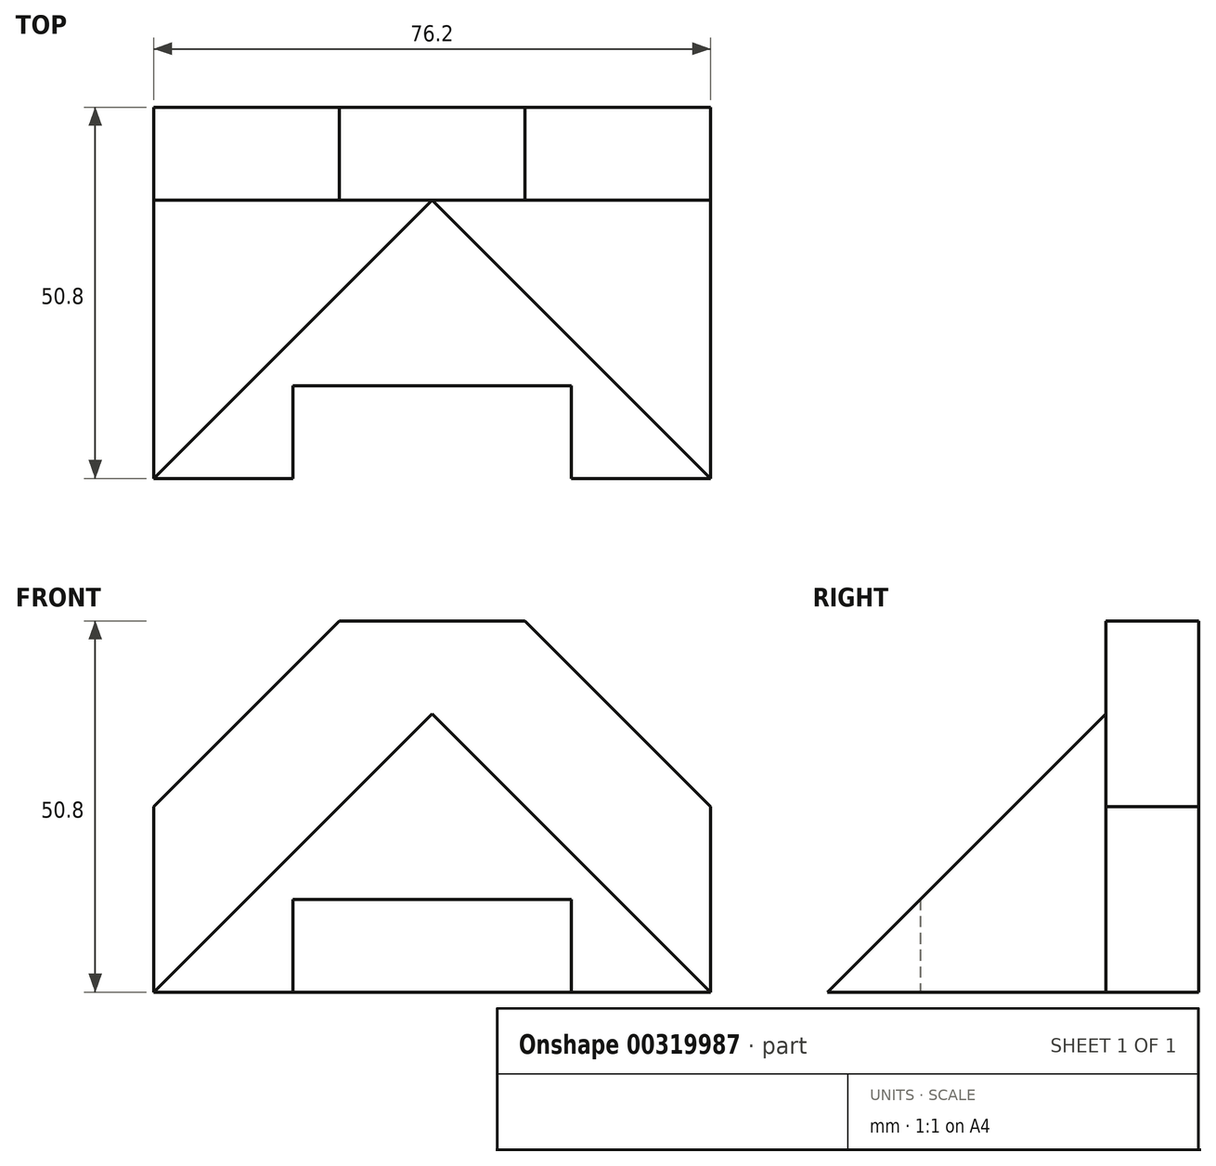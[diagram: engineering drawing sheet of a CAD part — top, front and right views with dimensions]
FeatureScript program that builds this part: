
annotation { "Feature Type Name" : "Feature", "Feature Type Description" : "" }
export const myFeature = defineFeature(function(context is Context, id is Id, definition is map)
    precondition{}
    {
        {
            var Q0;
            Q0=qCreatedBy(makeId("Front.planeOp"),FACE);
            var sketch = newSketch(context, id + "F0", { "sketchPlane" : qUnion([Q0])});
            skLineSegment(sketch, "E0", {"start": v(0, 0) * mm, "end": v(0, 25.4) * mm});
            skLineSegment(sketch, "E1", {"start": v(0, 25.4) * mm, "end": v(25.4, 50.8) * mm});
            skLineSegment(sketch, "E2", {"start": v(25.4, 50.8) * mm, "end": v(50.8, 50.8) * mm});
            skLineSegment(sketch, "E3", {"start": v(50.8, 50.8) * mm, "end": v(76.2, 25.4) * mm});
            skLineSegment(sketch, "E4", {"start": v(76.2, 25.4) * mm, "end": v(76.2, 0) * mm});
            skLineSegment(sketch, "E5", {"start": v(76.2, 0) * mm, "end": v(0, 0) * mm});
            skLineSegment(sketch, "E6", {"start": v(0, 0) * mm, "end": v(38.1, 38.1) * mm});
            skLineSegment(sketch, "E7", {"start": v(38.1, 38.1) * mm, "end": v(76.2, 0) * mm});
            skLineSegment(sketch, "E8", {"start": v(38.1, 50.8) * mm, "end": v(38.1, 0) * mm, "construction": true});
            skSolve(sketch);
        }
        {
            var Q0;
            Q0=makeQuery(id+"F0.imprint","IMPRINT",FACE,{"disambiguationData":[TD([[makeQuery(id+"F0.imprint","IMPRINT",EDGE,{"derivedFrom":sQuery(id+"F0.wireOp",EDGE,"E0")}),-1.0]])]});
            extrude(context, id + "F1", {"entities" : qUnion([Q0]), "depth" : 12.7 * mm});
        }
        {
            var Q0;
            Q0=makeQuery(id+"F0.imprint","IMPRINT",FACE,{"disambiguationData":[TD([[makeQuery(id+"F0.imprint","IMPRINT",EDGE,{"derivedFrom":sQuery(id+"F0.wireOp",EDGE,"E5")}),-1.0]])]});
            extrude(context, id + "F2", {"entities" : qUnion([Q0]), "operationType" : NewBodyOperationType.ADD, "depth" : 50.8 * mm});
        }
        {
            var Q0;
            Q0=qCreatedBy(makeId("Top.planeOp"),FACE);
            var sketch = newSketch(context, id + "F3", { "sketchPlane" : qUnion([Q0])});
            skLineSegment(sketch, "E9.bottom", {"start": v(19.05, -50.8) * mm, "end": v(57.15, -50.8) * mm});
            skLineSegment(sketch, "E9.top", {"start": v(19.05, -38.1) * mm, "end": v(57.15, -38.1) * mm});
            skLineSegment(sketch, "E9.left", {"start": v(19.05, -50.8) * mm, "end": v(19.05, -38.1) * mm});
            skLineSegment(sketch, "E9.right", {"start": v(57.15, -50.8) * mm, "end": v(57.15, -38.1) * mm});
            skSolve(sketch);
        }
        {
            var Q0;
            Q0=makeQuery(id+"F3.imprint","IMPRINT",FACE,{"disambiguationData":[TD([[makeQuery(id+"F3.imprint","IMPRINT",EDGE,{"derivedFrom":sQuery(id+"F3.wireOp",EDGE,"E9.bottom")}),1.0]])]});
            extrude(context, id + "F4", {"entities" : qUnion([Q0]), "operationType" : NewBodyOperationType.REMOVE, "depth" : 12.7 * mm});
        }
        {
            var Q0;
            {var subQ0=sQuery(id+"F0.wireOp",EDGE,"E5");var subQ1=sQuery(id+"F0.wireOp",EDGE,"E7");Q0=makeQuery(id+"F4.boolean.opBoolean","SPLIT",EDGE,{"disambiguationData":[TD([makeQuery(id+"F2.opExtrude","SWEPT_FACE",FACE,{"disambiguationData":[OSD([subQ1])]})])],"derivedFrom":makeQuery(id+"F2.opExtrude","CAP_EDGE",EDGE,{"disambiguationData":[OSD([subQ0])],"isStart":false})});}
            cPlane(context, id + "F5", {"entities" : qUnion([Q0]), "cplaneType" : CPlaneType.LINE_ANGLE, "offset" : 25.4 * mm, "angle" : 45 * degree, "width" : 152.4 * mm, "height" : 152.4 * mm});
        }
        {
            var Q0;
            Q0=qCreatedBy(id+"F5.planeOp",FACE);
            var sketch = newSketch(context, id + "F6", { "sketchPlane" : qUnion([Q0])});
            skLineSegment(sketch, "E10.0", {"start": v(0, -35.92) * mm, "end": v(38.1, -8.98) * mm});
            skLineSegment(sketch, "E11.0", {"start": v(38.1, -8.98) * mm, "end": v(76.2, -35.92) * mm});
            skLineSegment(sketch, "E12.0", {"start": v(38.1, 17.96) * mm, "end": v(76.2, -8.98) * mm});
            skLineSegment(sketch, "E13.0", {"start": v(0, -8.98) * mm, "end": v(38.1, 17.96) * mm});
            skLineSegment(sketch, "E14", {"start": v(0, -35.92) * mm, "end": v(38.1, 17.96) * mm});
            skLineSegment(sketch, "E15", {"start": v(76.2, -35.92) * mm, "end": v(38.1, 17.96) * mm});
            skLineSegment(sketch, "E16", {"start": v(0, -35.92) * mm, "end": v(76.2, -35.92) * mm});
            skSolve(sketch);
        }
        {
            var Q0;
            Q0 = qSketchRegion(id + "F6", true);
            extrude(context, id + "F7", {"entities" : qUnion([Q0]), "operationType" : NewBodyOperationType.REMOVE, "endBound" : BoundingType.THROUGH_ALL, "depth" : 25.4 * mm});
        }
    });
